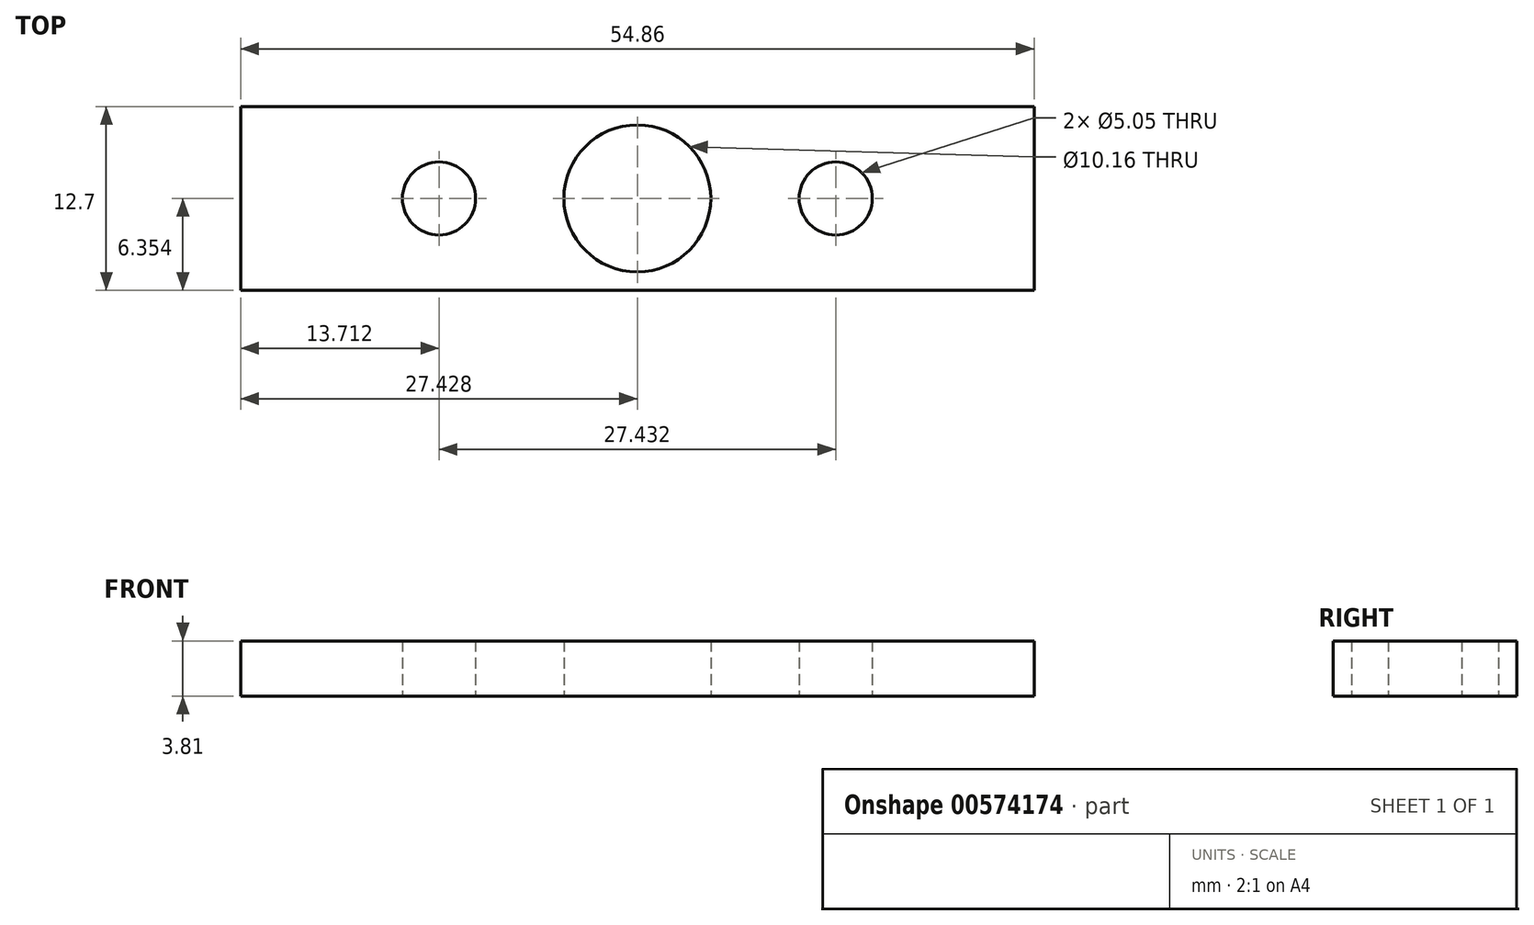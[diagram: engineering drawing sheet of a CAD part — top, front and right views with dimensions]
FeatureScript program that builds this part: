
annotation { "Feature Type Name" : "Feature", "Feature Type Description" : "" }
export const myFeature = defineFeature(function(context is Context, id is Id, definition is map)
    precondition{}
    {
        {
            var Q0;
            Q0=qCreatedBy(makeId("Top.planeOp"),FACE);
            var sketch = newSketch(context, id + "F0", { "sketchPlane" : qUnion([Q0])});
            skLineSegment(sketch, "E0.bottom", {"start": v(-54.86, -19.4) * mm, "end": v(0, -19.4) * mm});
            skLineSegment(sketch, "E0.top", {"start": v(-54.86, -6.7) * mm, "end": v(0, -6.7) * mm});
            skLineSegment(sketch, "E0.left", {"start": v(-54.86, -19.4) * mm, "end": v(-54.86, -6.7) * mm});
            skLineSegment(sketch, "E0.right", {"start": v(0, -19.4) * mm, "end": v(0, -6.7) * mm});
            skCircle(sketch, "E1", {"center": v(-27.43, -13.05) * mm, "radius": 5.08 * mm});
            skCircle(sketch, "E2", {"center": v(-41.15, -13.05) * mm, "radius": 2.53 * mm});
            skCircle(sketch, "E3", {"center": v(-13.72, -13.05) * mm, "radius": 2.53 * mm});
            skSolve(sketch);
        }
        {
            var Q0;
            Q0 = qSketchRegion(id + "F0", true);
            extrude(context, id + "F1", {"entities" : qUnion([Q0]), "depth" : 3.8 * mm, "offsetDistance" : 25.4 * mm});
        }
    });
